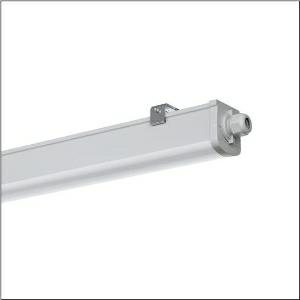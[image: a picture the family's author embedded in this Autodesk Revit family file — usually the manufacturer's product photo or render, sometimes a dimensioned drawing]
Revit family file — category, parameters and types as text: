
# Revit family: monsun_31_51fa20dk430b
name_source: partatom
category: Lighting Fixtures
units: mm (PartAtom-declared; Revit-internal decimal feet)

## family parameters
Cut with Voids When Loaded = No
Host = Face
Light Source = No
Part Type = Normal
Room Calculation Point = No
Round Connector Dimension = Use Diameter
Shared = No

## types (1)
- Monsun 31 (1 x LED, 3000 lm, 22 W, 4000K)
    Apparent Load = 22 VA
    CIE Flux Codes = 42 72 91 92 100
    Color Rendering = 80
    Color Temperature = 4000K
    Default Elevation = 1800 mm
    Description = Monsun 31, damp-proof luminaire, primary optical cover: diffuser, of PC, frosted, light emission: direct distribution, primary light characteristic: symmetric, installation type: surface-mounted, LED, rated luminous flux: 3.000lm, luminous efficacy: 136lm/W, light colour: 840, colour temperature: 4000K, control gear: DALI 2, with terminal, 5+1-pole, max. 2.5mm², through-wiring: 3x 2.5mm² + 3x 1.5mm², mains connection: 220..240V, AC, 50/60Hz, rated input power: 22W, housing, luminaire housing, of PC, light grey (RAL 7035), length: 1.158mm, width: 68mm, height: 76mm, protection rating (complete): IP66, insulation class (complete): insulation class II (safety insulation), certification: CE, ENEC, UKCA, protection symbol: D, impact resistance: IK08, permissible operating ambient temperature: -20..+40°C, corresponds to IFS (International Featured Standards) requirements for safety and quality in the food industry, contact your sales advisor before using the luminaires in applications with unclear chemical exposure, large temperature fluctuations or condensation-forming humidity, packaging unit: 1 piece
    Height = 77 mm
    Lamp = 1 x LED
    Lamp Light Flux = 3000 lm
    Lamp Power = 22 W
    Lamp count = 1
    Length = 1218 mm
    Luminous efficacy = 136 lm/W
    Manufacturer = Siteco
    ModVariant = No
    Model = 51FA20DK430B
    Mounting Place = Ceiling
    Mounting Type = Surface mounted
    Number of Poles = 1
    OnlyDefault = Yes
    Power Factor = 1
    Product Name = Monsun 31
    Product group = damp-proof luminaire
    ProductGroupID = 300
    Protection Class = Protection class II
    Protection Degree = IP 66
    RLX_Detail_Level = 1
    RLX_Emergency_Light_Flux = 0 lm
    RLX_Emergency_Type = 0
    RLX_Emergency_Type_DB = No
    RlxData = <blob elided: 32937 chars, md5=4c792119>
    Socket = socket
    Standby Power = 0 W
    System Light Flux = 3000 lm
    System Power = 22 W
    Type Comments = Product without accessories
    Type Image = l_1006174.jpg
    URL = http://relux.com
    VarID = ---
    Voltage = 0 V
    Weight = 0.00 kg
    Width = 69 mm

## geometry (parser evidence)
native form markers: Blend x4, Sweep x12
no freeform markers — native parametric forms only
